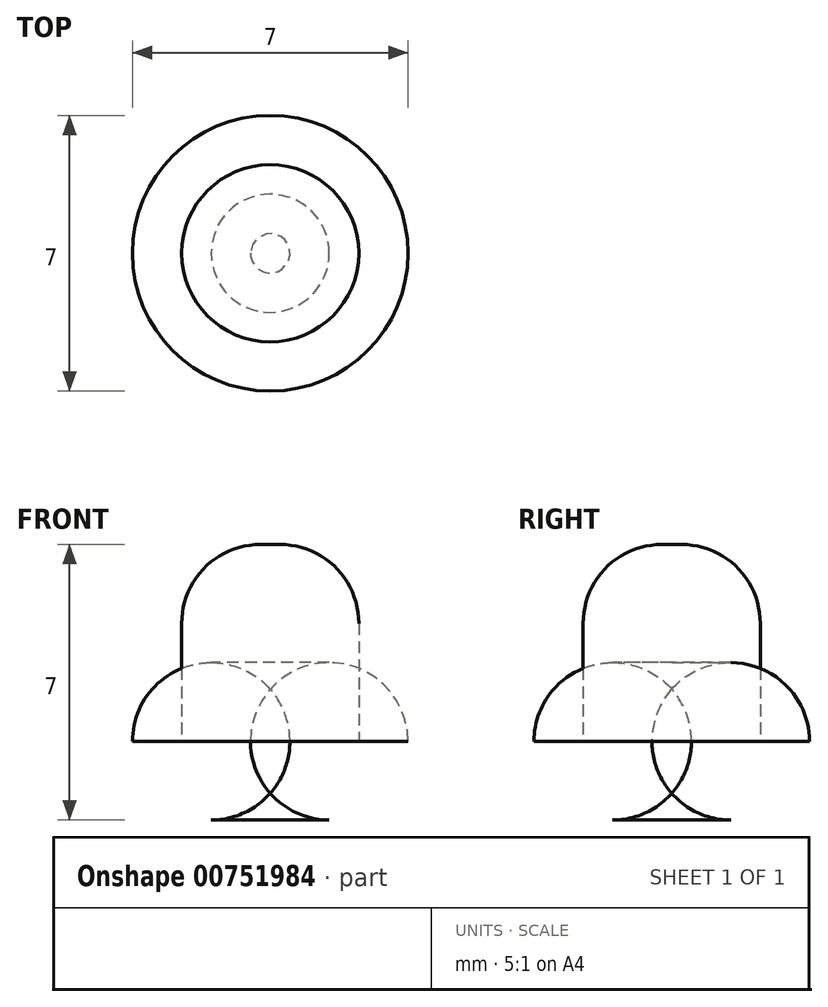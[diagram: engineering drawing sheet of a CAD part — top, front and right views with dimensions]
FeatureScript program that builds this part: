
annotation { "Feature Type Name" : "Feature", "Feature Type Description" : "" }
export const myFeature = defineFeature(function(context is Context, id is Id, definition is map)
    precondition{}
    {
        {
            var Q0;
            Q0=qCreatedBy(makeId("Top.planeOp"),FACE);
            var sketch = newSketch(context, id + "F0", { "sketchPlane" : qUnion([Q0])});
            skCircle(sketch, "E0", {"center": v(0, 0) * mm, "radius": 3.5 * mm});
            skCircle(sketch, "E1", {"center": v(0, 0) * mm, "radius": 2.25 * mm});
            skSolve(sketch);
        }
        {
            var Q0;
            Q0=makeQuery(id+"F0.imprint","IMPRINT",FACE,{"disambiguationData":[TD([[makeQuery(id+"F0.imprint","IMPRINT",EDGE,{"derivedFrom":sQuery(id+"F0.wireOp",EDGE,"E1")}),1.0]])]});
            var Q1;
            Q1=makeQuery(id+"F0.imprint","IMPRINT",FACE,{"disambiguationData":[TD([[makeQuery(id+"F0.imprint","IMPRINT",EDGE,{"derivedFrom":sQuery(id+"F0.wireOp",EDGE,"E0")}),1.0]])]});
            extrude(context, id + "F1", {"entities" : qUnion([Q0, Q1]), "oppositeDirection" : true, "depth" : 2 * mm, "offsetDistance" : 25 * mm});
        }
        {
            var Q0;
            Q0=makeQuery(id+"F0.imprint","IMPRINT",FACE,{"disambiguationData":[TD([[makeQuery(id+"F0.imprint","IMPRINT",EDGE,{"derivedFrom":sQuery(id+"F0.wireOp",EDGE,"E1")}),1.0]])]});
            extrude(context, id + "F2", {"entities" : qUnion([Q0]), "operationType" : NewBodyOperationType.ADD, "depth" : 5 * mm, "offsetDistance" : 25 * mm});
        }
        {
            var Q0;
            Q0=makeQuery(id+"F2.opExtrude","CAP_EDGE",EDGE,{"disambiguationData":[OSD([sQuery(id+"F0.wireOp",EDGE,"E1")])],"isStart":false});
            var Q1;
            Q1=makeQuery(id+"F1.opExtrude","CAP_EDGE",EDGE,{"disambiguationData":[OSD([sQuery(id+"F0.wireOp",EDGE,"E0")])],"isStart":false});
            fillet(context, id + "F3", {"entities" : qUnion([Q0, Q1]), "radius" : 2 * mm, "tangentPropagation" : true, "allowEdgeOverflow" : false});
        }
    });
